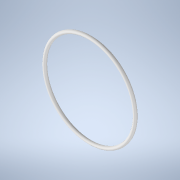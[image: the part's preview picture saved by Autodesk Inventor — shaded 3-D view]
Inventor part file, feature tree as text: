
AUTODESK INVENTOR PART (.ipt)
format: ipt  version: 2022 (Build 260153000, 153)  size: 118,784 bytes
history: native  units: mm
features: revolve x1, sketch x1
ambient origin geometry x8: Origin, YZ Plane, XZ Plane, XY Plane, X Axis, Y Axis, Z Axis, Center Point
bodies: Volumenkörper1 (feature_tree)
feature tree (2):
  revolve  "Umdrehung1"
  sketch  "Skizze1"  dims[d2=90.0deg d4=26.5mm]
